# Revit family: Faucet-Two_Handle-American_Standard-Monterrey-65401X0_Series.rfaxxxx
name_source: partatom
category: Plumbing Fixtures
units: mm (PartAtom-declared; Revit-internal decimal feet)

## family parameters
Always vertical = No
Cut with Voids When Loaded = No
OmniClass Number = 23.45.55.17
OmniClass Title = Mixing Faucets
Part Type = Normal
Room Calculation Point = No
Round Connector Dimension = Use Diameter
Shared = Yes
Work Plane-Based = Yes

## types (2) — shared parameters
ADA Compliant = Yes
Assembly Code = D2020300
CW Connection = Yes
CWFU = 1.5
Cold Water Connection Diameter = 1/2"
Compliance Certifications = ASME A112.18.1, CSA B125.1 and NSF 372
Default Elevation = 0"
Finish = Cast Brass-American Standard-002-Polished Chrome
Flow Rate = 1.5 gpm/5.7 Lpm
HW Connection = Yes
HWFU = 1.5
Handle Distance = 8"
Height = 10 5/8"
Hot Water Connection Diameter = 1/2"
Installation Type = Deck Mounted
Manufacturer = American Standard
Material = Cast Brass-American Standard-002-Polished Chrome
Pop-up Drain Depth = 5"
Pop-up Drain Included = Yes
Pop-up Drain Width from Faucet Centre Constraint = 3"
Price = Prices may vary. Please consult Manufacturer Representative for most up-to-date price list.
Product Documentation Link = https://americanstandard.box.com
Product Page URL = https://americanstandard.ca
Reach Height = 6 1/2"
Revised Date = 07/25/2022
Spout Reach = 5"
URL = https://americanstandard.ca
Vent Connection = No
WFU = 2
Warranty Information = 5 Year Limited Warranty
Waste Connection = No

## per-type parameters (varying)
| type | Description | Length | Lever Handles | Wrist Blade Handles |
| 6540.170.002 | Monterrey® 8-Inch Widespread Gooseneck Faucet With Wrist Blade Handles 1.5 gpm/5.7 Lpm | 15 3/4" | No | Yes |
| 6540.140.002 | Monterrey® 8-Inch Widespread Gooseneck Faucet With Lever Handles 1.5 gpm/5.7 Lpm | 12 1/2" | Yes | No |

note: column(s) folded — value = type name in every type: Model

## geometry (parser evidence)
native form markers: Sweep x2
no freeform markers — native parametric forms only
